# Revit family: Stenos 12in Downlight at 3500K, 55deg Beam, White
name_source: partatom
category: Lighting Fixtures
units: mm (PartAtom-declared; Revit-internal decimal feet)

## family parameters
Cut with Voids When Loaded = No
Host = Face
Light Source = Yes
OmniClass Number = 23.80.70.11.14.21
OmniClass Title = Spots and Tracklight Specialties
Part Type = Normal
Room Calculation Point = No
Round Connector Dimension = Use Diameter
Shared = Yes

## types (1)
- SD-12-35K-SO-55-WH
    Apparent Load = 120 VA
    Assembly Code = D5020230
    CCT = 3500K
    CRI = 97
    Color Filter = 16777215
    Current Amps = 0 A
    Default Elevation = 4' - 0"
    Depth = 0' - 1 31/32"
    Description = Linear Illumination System
    Dimming Lamp Color Temperature Shift = <None>
    Emit Shape Visible in Rendering = Yes
    Emit from Rectangle Length = 0' - 11 5/8"
    Emit from Rectangle Width = 0' - 0 3/4"
    Environment = Damp
    Finish = Paint - Luminii - Black
    Frequency = 0 Hz
    Has Battery Backup = No
    Has Dimming = No
    Housing Protection Rating = IP20 Dry/IP66 Wet Series
    Initial Color Comments = Perfomance based on 3500K Photometric Web File
    Lamp = LED
    Lamp Life = 1
    Lens Material = Plastic - Luminii - Frosted Lens
    Lens Width = 0' - 0 17/32"
    Load Classification = Lighting
    Lumen Output = 1260 Lumens
    Manufacturer = Luminii
    Model = SD-12-35K-SO-55-WH
    Mounting Method = Recessed
    Number of Poles = 1
    Phase = 1
    Photometric Web File = SD-12-35K-SO-55-WH (calc).ies
    Power Factor = 1
    Power Source Type = Driver
    Product Documentation Link = https://www.luminii.com
    Product Name = Stenos Downlight
    Product Page URL = https://www.luminii.com
    Tilt Angle = 0.00°
    URL = https://www.luminii.com
    Version = 2020 - v1.0a
    Voltage = 24 V
    Voltage Comments = 120-277VAC
    Warranty URL = https://www.luminii.com
    Wattage Comments = 13 watts
    Width = 0' - 0 27/32"

## geometry (parser evidence)
native form markers: Sweep x1
no freeform markers — native parametric forms only
